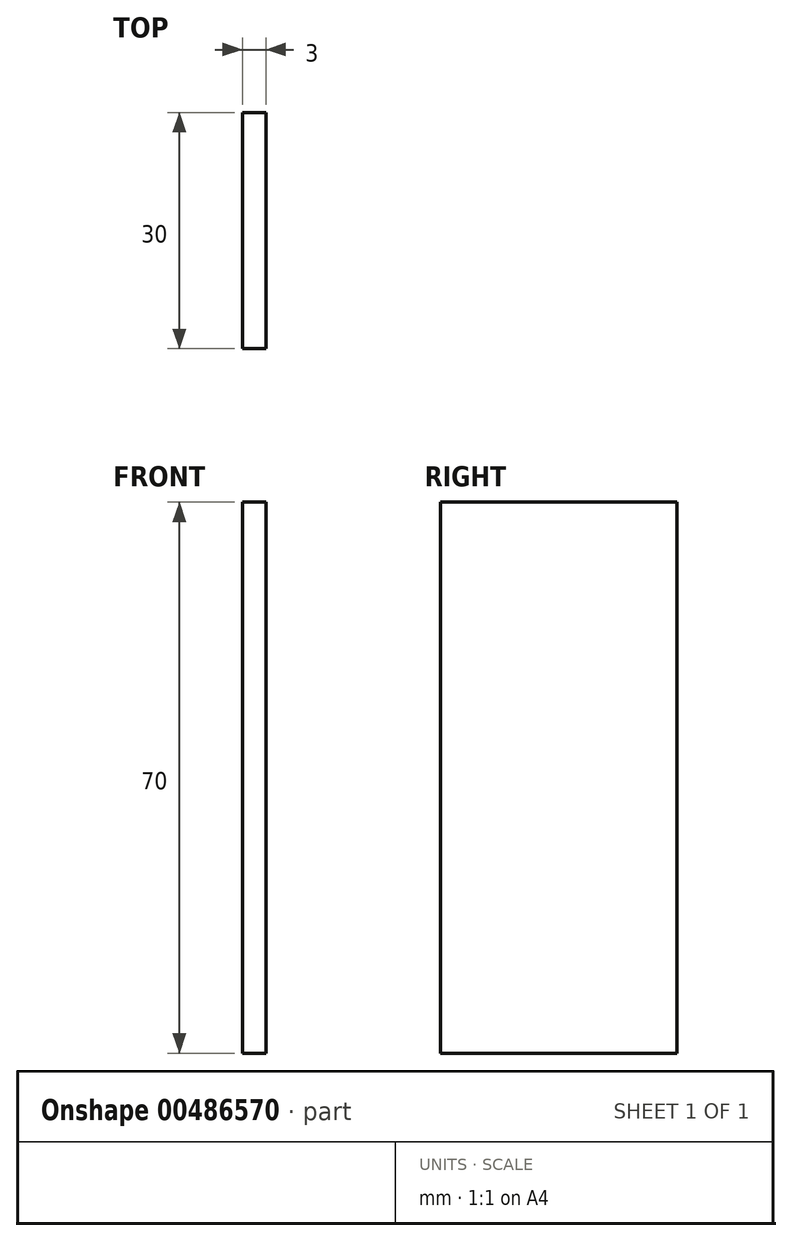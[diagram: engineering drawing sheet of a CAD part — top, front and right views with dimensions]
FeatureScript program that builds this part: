
annotation { "Feature Type Name" : "Feature", "Feature Type Description" : "" }
export const myFeature = defineFeature(function(context is Context, id is Id, definition is map)
    precondition{}
    {
        {
            var Q0;
            Q0=qCreatedBy(makeId("Top.planeOp"),FACE);
            var sketch = newSketch(context, id + "F0", { "sketchPlane" : qUnion([Q0])});
            skLineSegment(sketch, "E0.bottom", {"start": v(0, 0) * mm, "end": v(3, 0) * mm});
            skLineSegment(sketch, "E0.top", {"start": v(0, 30) * mm, "end": v(3, 30) * mm});
            skLineSegment(sketch, "E0.left", {"start": v(0, 0) * mm, "end": v(0, 30) * mm});
            skLineSegment(sketch, "E0.right", {"start": v(3, 0) * mm, "end": v(3, 30) * mm});
            skSolve(sketch);
        }
        {
            var Q0;
            Q0=makeQuery(id+"F0.imprint","IMPRINT",FACE,{"disambiguationData":[TD([[makeQuery(id+"F0.imprint","IMPRINT",EDGE,{"derivedFrom":sQuery(id+"F0.wireOp",EDGE,"E0.bottom")}),1.0]])]});
            extrude(context, id + "F1", {"entities" : qUnion([Q0]), "depth" : 70 * mm});
        }
    });
